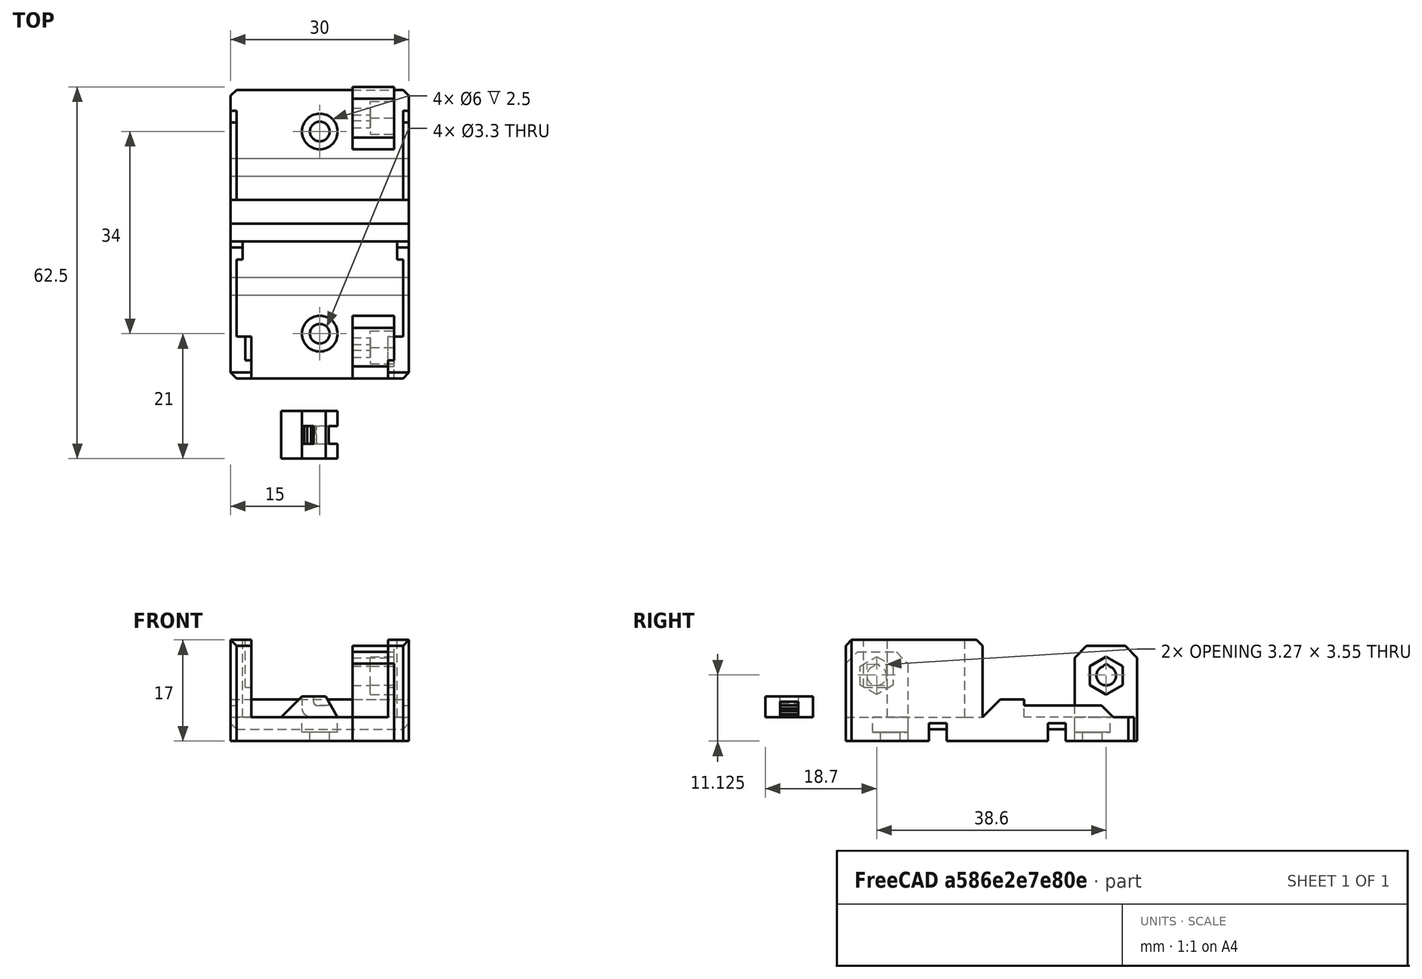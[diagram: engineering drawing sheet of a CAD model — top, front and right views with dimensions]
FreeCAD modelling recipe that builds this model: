
FCSTD DOCUMENT  (FreeCAD 0.18R14555 (Git shallow))
Label: prusa-power-connectore
License: All rights reserved
LicenseURL: http://en.wikipedia.org/wiki/All_rights_reserved
objects: Part::Box×16, Part::Cut×10, Part::Cylinder×8, Part::Chamfer×7, Part::MultiFuse×5, Part::Feature×4
note: 50 computed .brp shape members not serialized (recipe doc carries the construction recipe); baked Part::Feature solids carry a one-line shape summary decoded from their .brp

FEATURE [Part::Box] Box  label="Cube"
  AttacherType = Attacher::AttachEngine3D
  Height = 4
  Length = 30
  Placement = pos=(0,-24.5,0) rot=(0,0,1;0rad)
  Width = 48.5
FEATURE [Part::Box] Box001  label="Cube001"
  AttacherType = Attacher::AttachEngine3D
  Height = 16
  Length = 7
  Placement = pos=(20.5,14,0) rot=(0,0,1;0rad)
  Width = 10.5
FEATURE [Part::Feature] Body001
  Placement = pos=(23.5,19.3,11) rot=(0,0,1;0rad)
  shape: bbox 10 x 5.543 x 6.4 mm, 8 faces (baked)
FEATURE [Part::Feature] Body002
  Placement = pos=(23.5,-19.3,11) rot=(0,0,1;0rad)
  shape: bbox 10 x 5.543 x 6.4 mm, 8 faces (baked)
FEATURE [Part::Box] Box002  label="Cube002"
  AttacherType = Attacher::AttachEngine3D
  Height = 15
  Length = 7
  Placement = pos=(20.5,-24.5,0) rot=(0,0,1;0rad)
  Width = 10.5
FEATURE [Part::Cylinder] Cylinder
  Angle = 360
  AttacherType = Attacher::AttachEngine3D
  Height = 10
  Placement = pos=(20.5,19.3,12.4) rot=(0,1,0;1.5708rad)
  Radius = 0.5
FEATURE [Part::Cylinder] Cylinder001
  Angle = 360
  AttacherType = Attacher::AttachEngine3D
  Height = 10
  Placement = pos=(20.5,-19.3,12.4) rot=(0,1,0;1.5708rad)
  Radius = 0.5
FEATURE [Part::Cylinder] Cylinder002
  Angle = 360
  AttacherType = Attacher::AttachEngine3D
  Height = 10
  Placement = pos=(20.5,19.3,11) rot=(0,1,0;1.5708rad)
  Radius = 1.65
FEATURE [Part::Cylinder] Cylinder003
  Angle = 360
  AttacherType = Attacher::AttachEngine3D
  Height = 10
  Placement = pos=(20.5,-19.3,11) rot=(0,1,0;1.5708rad)
  Radius = 1.65
FEATURE [Part::Cut] Cut
  Base = -> Box001
  Tool = -> Cylinder002
FEATURE [Part::Cut] Cut001
  Base = -> Box002
  Tool = -> Cylinder003
FEATURE [Part::Cut] Cut002
  Base = -> Cut
  Tool = -> Cylinder
FEATURE [Part::Cut] Cut003
  Base = -> Cut001
  Tool = -> Cylinder001
FEATURE [Part::Cut] Cut004
  Base = -> Cut002
  Tool = -> Body001
FEATURE [Part::Cut] Cut005
  Base = -> Cut003
  Tool = -> Body002
FEATURE [Part::Chamfer] Chamfer
  Base = -> Cut005
  Edges = 2 edges r=2: [Edge10,Edge11]
FEATURE [Part::Chamfer] Chamfer001
  Base = -> Cut004
  Edges = 2 edges r=2: [Edge10,Edge11]
FEATURE [Part::Box] Box003  label="Cube003"
  AttacherType = Attacher::AttachEngine3D
  Height = 17
  Length = 3.5
  Placement = pos=(0,-24.5,0) rot=(0,0,1;0rad)
  Width = 7
FEATURE [Part::Box] Box004  label="Cube004"
  AttacherType = Attacher::AttachEngine3D
  Height = 17
  Length = 3.5
  Placement = pos=(26.5,-24.5,0) rot=(0,0,1;0rad)
  Width = 7
FEATURE [Part::Box] Box005  label="Cube005"
  AttacherType = Attacher::AttachEngine3D
  Height = 17
  Length = 1
  Placement = pos=(0,-17.5,0) rot=(0,0,1;0rad)
  Width = 13
FEATURE [Part::Box] Box006  label="Cube006"
  AttacherType = Attacher::AttachEngine3D
  Height = 17
  Length = 1
  Placement = pos=(29,-17.5,0) rot=(0,0,1;0rad)
  Width = 13
FEATURE [Part::Box] Box007  label="Cube007"
  AttacherType = Attacher::AttachEngine3D
  Height = 17
  Length = 2
  Placement = pos=(0,-4.5,0) rot=(0,0,1;0rad)
  Width = 3
FEATURE [Part::Box] Box008  label="Cube008"
  AttacherType = Attacher::AttachEngine3D
  Height = 17
  Length = 2
  Placement = pos=(28,-4.5,0) rot=(0,0,1;0rad)
  Width = 3
FEATURE [Part::Box] Box009  label="Cube009"
  AttacherType = Attacher::AttachEngine3D
  Height = 8
  Length = 1
  Placement = pos=(2.5,-21.5,9) rot=(0,0,1;0rad)
  Width = 4
FEATURE [Part::Box] Box010  label="Cube010"
  AttacherType = Attacher::AttachEngine3D
  Height = 8
  Length = 1
  Placement = pos=(26.5,-21.5,9) rot=(0,0,1;0rad)
  Width = 4
FEATURE [Part::Cut] Cut006
  Base = -> Box004
  Tool = -> Box010
FEATURE [Part::Cut] Cut007
  Base = -> Box003
  Tool = -> Box009
FEATURE [Part::MultiFuse] Fusion
  Shapes = -> [Cut007,Box005,Box007]
FEATURE [Part::MultiFuse] Fusion001
  Shapes = -> [Cut006,Box006,Box008]
FEATURE [Part::Feature] Part__Feature  label="Common002"
  Placement = pos=(-12,-15.5,66.75) rot=(0.57735,-0.57735,0.57735;4.18879rad)
  shape: bbox 9.5 x 8 x 3.5 mm, 30 faces (baked)
FEATURE [Part::Box] Box011  label="Cube011"
  AttacherType = Attacher::AttachEngine3D
  Height = 2
  Length = 36
  Placement = pos=(-3,-10.5,0) rot=(0,0,1;0rad)
  Width = 3
FEATURE [Part::Box] Box012  label="Cube012"
  AttacherType = Attacher::AttachEngine3D
  Height = 2
  Length = 36
  Placement = pos=(-3,9.5,0) rot=(0,0,1;0rad)
  Width = 3
FEATURE [Part::Cylinder] Cylinder004
  Angle = 360
  AttacherType = Attacher::AttachEngine3D
  Height = 2.5
  Placement = pos=(15,17,1.5) rot=(0,0,1;0rad)
  Radius = 3
FEATURE [Part::Cylinder] Cylinder005
  Angle = 360
  AttacherType = Attacher::AttachEngine3D
  Height = 2.5
  Placement = pos=(15,-17,1.5) rot=(0,0,1;0rad)
  Radius = 3
FEATURE [Part::Cylinder] Cylinder006
  Angle = 360
  AttacherType = Attacher::AttachEngine3D
  Height = 10
  Placement = pos=(15,-17,0) rot=(0,0,1;0rad)
  Radius = 1.65
FEATURE [Part::Cylinder] Cylinder007
  Angle = 360
  AttacherType = Attacher::AttachEngine3D
  Height = 10
  Placement = pos=(15,17,0) rot=(0,0,1;0rad)
  Radius = 1.65
FEATURE [Part::Box] Box013  label="Cube013"
  AttacherType = Attacher::AttachEngine3D
  Height = 7
  Length = 30
  Placement = pos=(0,-1.5,0) rot=(0,0,1;0rad)
  Width = 7
FEATURE [Part::Chamfer] Chamfer002
  Base = -> Box013
  Edges = 1 edges r=3: [Edge10]
FEATURE [Part::Box] Box014  label="Cube014"
  AttacherType = Attacher::AttachEngine3D
  Height = 6
  Length = 1
  Placement = pos=(0,5.5,0) rot=(0,0,1;0rad)
  Width = 15
FEATURE [Part::Box] Box015  label="Cube015"
  AttacherType = Attacher::AttachEngine3D
  Height = 6
  Length = 1
  Placement = pos=(29,5.5,0) rot=(0,0,1;0rad)
  Width = 15
FEATURE [Part::MultiFuse] Fusion002
  Shapes = -> [Cylinder005,Cylinder004,Cylinder006,Cylinder007]
FEATURE [Part::MultiFuse] Fusion003
  Shapes = -> [Box011,Box012]
FEATURE [Part::Cut] Cut008
  Base = -> Box
  Tool = -> Fusion002
FEATURE [Part::Chamfer] Chamfer003
  Base = -> Box015
  Edges = 1 edges r=2: [Edge12]
FEATURE [Part::Chamfer] Chamfer004
  Base = -> Box014
  Edges = 1 edges r=2: [Edge12]
FEATURE [Part::MultiFuse] Fusion004
  Shapes = -> [Chamfer004,Chamfer003,Chamfer002,Cut008,Fusion001,Fusion]
FEATURE [Part::Cut] Cut009
  Base = -> Fusion004
  Tool = -> Fusion003
FEATURE [Part::Chamfer] Chamfer005
  Base = -> Cut009
  Edges = 4 edges r=1: [Edge11,Edge39,Edge124,Edge178]
FEATURE [Part::Chamfer] Chamfer006
  Base = -> Chamfer005
  Edges = 10 edges r=1: [Edge31,Edge64,Edge127,Edge141,Edge164,Edge216,Edge223,Edge230,Edge235,Edge239]
FEATURE [Part::Feature] Chamfer006001  label="Chamfer007"
  shape: bbox 30 x 48.5 x 17 mm, 62 faces (baked)
